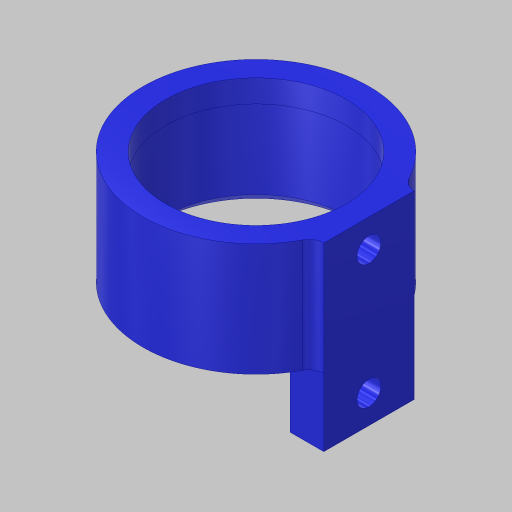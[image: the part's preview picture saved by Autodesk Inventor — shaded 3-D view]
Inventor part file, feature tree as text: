
AUTODESK INVENTOR PART (.ipt)
format: ipt  version: 2023.5 (Build 275446000, 446)  size: 187,392 bytes
history: native  units: in
note: dims shown in document units (in); Inventor stores cm internally (conversion verified against a paired STEP export)
features: extrude x4, sketch x3, chamfer x2, plane x1, fillet x1, mirror x1, projected_geometry x1
ambient origin geometry x8: Origin, YZ Plane, XZ Plane, XY Plane, X Axis, Y Axis, Z Axis, Center Point
bodies: Solid1 (feature_tree)
feature tree (13):
  extrude  "Extrusion1"  Depth=2.0in
  extrude  "Extrusion2"  Depth=1.0in
  chamfer  "Chamfer1"  Distance=1.0in
  plane  "Work Plane1"
  sketch  "Sketch5"  dims[d21=0.125in d22=0.125in d23=45.0deg d27=2.5in d28=2.0in d29=0.2638in d30=0.25in d31=0.0in d32=0.0312in d33=0.125in d34=45.0deg d35=1.0in d36=1.375in d37=2.0in d38=1.0in d39=0.0in d40=0.17in]
  extrude  "Extrusion4"  Depth=0.17in
  extrude  "Extrusion5"  Depth=2.0in
  fillet  "Fillet1"  Radius=0.2638in
  mirror  "Mirror1"
  chamfer  "Chamfer3"  Distance=0.25in
  sketch  "Sketch1"  dims[d0=2.0in d1=2.5in]
  sketch  "Sketch2"  dims[d2=0.25in d3=0.0in d4=2.02in d5=1.0in d6=0.0in]
  projected_geometry  "Projected Loop1"
